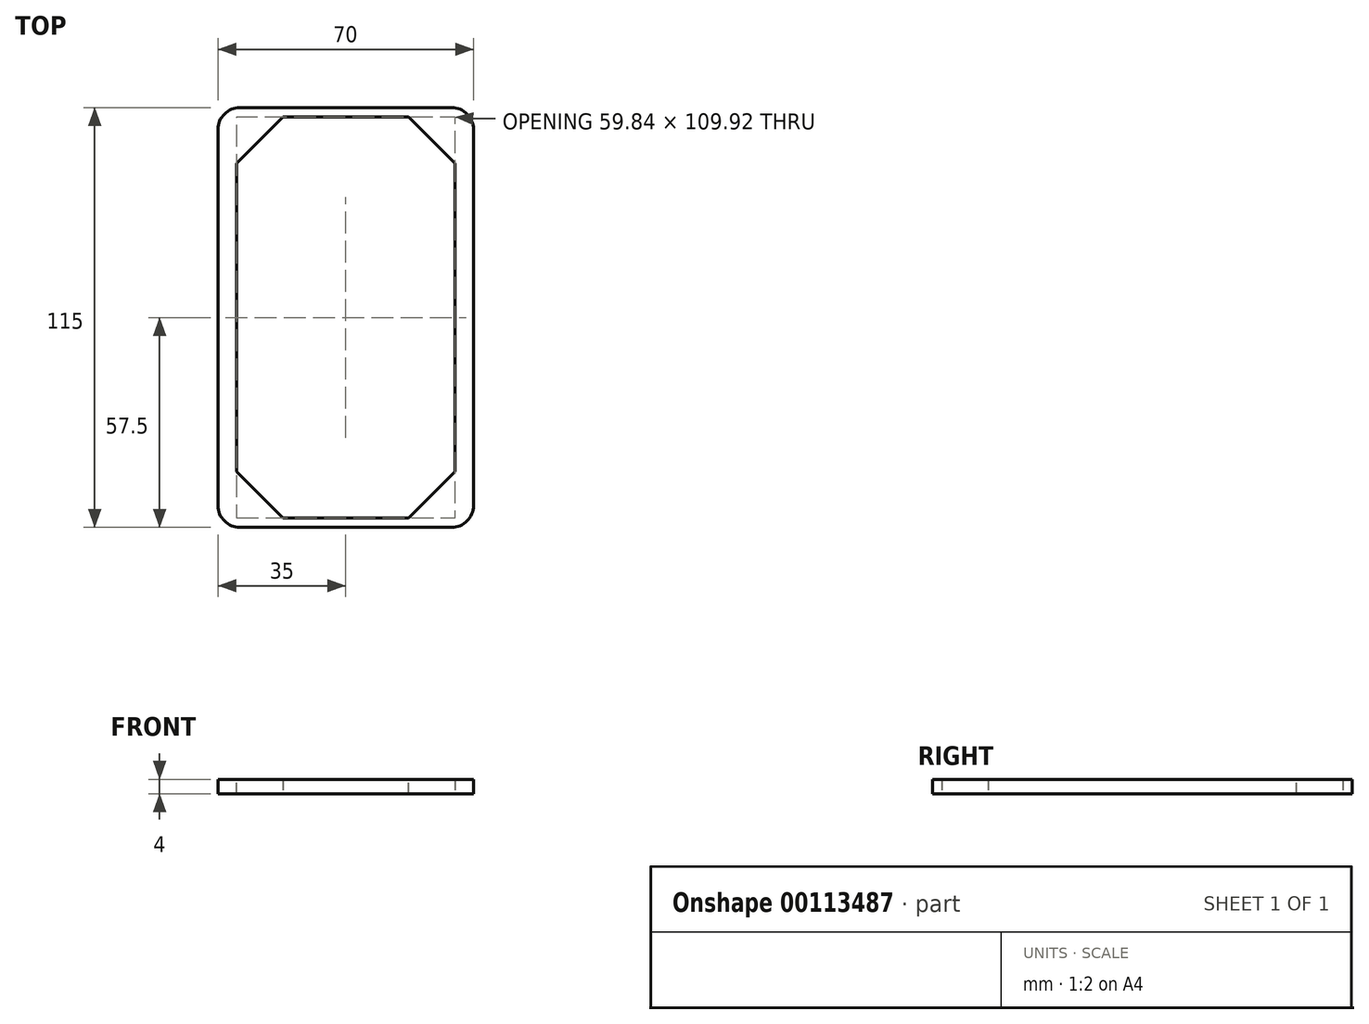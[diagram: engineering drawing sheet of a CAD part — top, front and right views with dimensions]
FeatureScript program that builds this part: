
annotation { "Feature Type Name" : "Feature", "Feature Type Description" : "" }
export const myFeature = defineFeature(function(context is Context, id is Id, definition is map)
    precondition{}
    {
        {
            var Q0;
            Q0=qCreatedBy(makeId("Top.planeOp"),FACE);
            var sketch = newSketch(context, id + "F0", { "sketchPlane" : qUnion([Q0])});
            skLineSegment(sketch, "E0.bottom", {"start": v(0, 0) * mm, "end": v(70, 0) * mm});
            skLineSegment(sketch, "E0.top", {"start": v(0, 115) * mm, "end": v(70, 115) * mm});
            skLineSegment(sketch, "E0.left", {"start": v(0, 0) * mm, "end": v(0, 115) * mm});
            skLineSegment(sketch, "E0.right", {"start": v(70, 0) * mm, "end": v(70, 115) * mm});
            skLineSegment(sketch, "E1.bottom", {"start": v(5.08, 112.46) * mm, "end": v(64.92, 112.46) * mm});
            skLineSegment(sketch, "E1.top", {"start": v(5.08, 2.54) * mm, "end": v(64.92, 2.54) * mm});
            skLineSegment(sketch, "E1.left", {"start": v(5.08, 112.46) * mm, "end": v(5.08, 2.54) * mm});
            skLineSegment(sketch, "E1.right", {"start": v(64.92, 112.46) * mm, "end": v(64.92, 2.54) * mm});
            skSolve(sketch);
        }
        {
            var Q0;
            Q0=qSketchRegion(id+"F0",true);
            extrude(context, id + "F1", {"entities" : qUnion([Q0]), "depth" : 4 * mm});
        }
        {
            var Q0;
            Q0=makeQuery(id+"F1.opExtrude","SWEPT_EDGE",EDGE,{"disambiguationData":[OSD([sQuery(id+"F0.wireOp",EDGE,"E0.top"),sQuery(id+"F0.wireOp",EDGE,"E0.left")])]});
            var Q1;
            Q1=makeQuery(id+"F1.opExtrude","SWEPT_EDGE",EDGE,{"disambiguationData":[OSD([sQuery(id+"F0.wireOp",EDGE,"E0.top"),sQuery(id+"F0.wireOp",EDGE,"E0.right")])]});
            var Q2;
            Q2=makeQuery(id+"F1.opExtrude","SWEPT_EDGE",EDGE,{"disambiguationData":[OSD([sQuery(id+"F0.wireOp",EDGE,"E0.bottom"),sQuery(id+"F0.wireOp",EDGE,"E0.right")])]});
            var Q3;
            Q3=makeQuery(id+"F1.opExtrude","SWEPT_EDGE",EDGE,{"disambiguationData":[OSD([sQuery(id+"F0.wireOp",EDGE,"E0.bottom"),sQuery(id+"F0.wireOp",EDGE,"E0.left")])]});
            fillet(context, id + "F2", {"entities" : qUnion([Q0, Q1, Q2, Q3]), "radius" : 6 * mm, "tangentPropagation" : true, "allowEdgeOverflow" : false});
        }
        {
            var Q0;
            Q0=makeQuery(id+"F1.opExtrude","SWEPT_EDGE",EDGE,{"disambiguationData":[OSD([sQuery(id+"F0.wireOp",EDGE,"E1.bottom"),sQuery(id+"F0.wireOp",EDGE,"E1.left")])]});
            var Q1;
            Q1=makeQuery(id+"F1.opExtrude","SWEPT_EDGE",EDGE,{"disambiguationData":[OSD([sQuery(id+"F0.wireOp",EDGE,"E1.top"),sQuery(id+"F0.wireOp",EDGE,"E1.right")])]});
            var Q2;
            Q2=makeQuery(id+"F1.opExtrude","SWEPT_EDGE",EDGE,{"disambiguationData":[OSD([sQuery(id+"F0.wireOp",EDGE,"E1.bottom"),sQuery(id+"F0.wireOp",EDGE,"E1.right")])]});
            var Q3;
            Q3=makeQuery(id+"F1.opExtrude","SWEPT_EDGE",EDGE,{"disambiguationData":[OSD([sQuery(id+"F0.wireOp",EDGE,"E1.top"),sQuery(id+"F0.wireOp",EDGE,"E1.left")])]});
            chamfer(context, id + "F3", {"entities" : qUnion([Q0, Q1, Q2, Q3]), "width" : 12.7 * mm, "tangentPropagation" : true});
        }
    });
